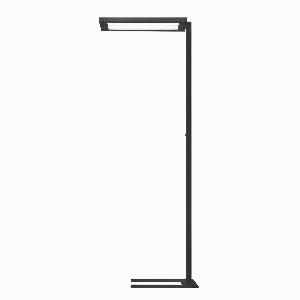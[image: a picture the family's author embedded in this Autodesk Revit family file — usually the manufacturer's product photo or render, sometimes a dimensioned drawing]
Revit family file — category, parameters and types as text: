
# Revit family: lavigo_core_-_dps_9000_840_r_g1_sw_00812472_8bfc
name_source: partatom
category: Lighting Fixtures
units: mm (PartAtom-declared; Revit-internal decimal feet)

## family parameters
Cut with Voids When Loaded = No
Host = Face
Light Source = No
Part Type = Normal
Room Calculation Point = No
Round Connector Dimension = Use Diameter
Shared = No

## types (1)
- LAVIGO.core - DPS 9000/840/R/G1/SW (1 x LED, 8900 lm, 4000K)
    Apparent Load = 62 VA
    Approval mark = CE
    CIE Flux Codes = 59 88 97 35 100
    Color Rendering = 80-89
    Color Temperature = 4000K
    Control Gear = Electronic ballast
    Default Elevation = 1800 mm
    Description = DPS 9000/840/R/G1|Free-standing luminaire|light source: LED Cold white   |work equipment: Electronic ballast DALI|connected load: 220-240 V, 50/60 Hz|Power consumption: approx. 62 W|standby: approx. 0,30|power factor: approx. 0,959|luminous flux: 8900 lm|luminous efficacy: 143 lm/W|light distribution: Direct/indirect|direct ratio: approx. 35 %|color rendering index (CRI): >= 80|chromaticity tolerance:  3 SDCM|technology: Presence and daylight sensor control (PIR)|operation: Rocker switch|luminaire body|material: Steel/plastic|surface: Painted|colour: Black|lamp cover: Polycarbonate (PC), Clear|tubular section|material: Steel tube|surface: Painted|Form: Tubular section upright|colour of tubular section: Black|luminaire base|Form: C-form flat|weight (net): approx. 14.7 kg|mains lead: 3.00 m Mains plug CEE 7/VII|Fastening: Floor standing base|decorative contrast side parts: Black|glare control: Prism aperture|luminance(L65): <= 4400 cd/m|unified glare rating(4H 8H): <=  16|special features: Luminaire head detachable, Direct and indirect light switchable together, Flicker-free, Integrated light and presence sensor PIR, Motion sensor time-out of 15mins~|Approval mark: US~B_0014~VDE - ENEC|
    Frequency = 50 Hz, 60 Hz
    Height = 36 mm
    Lamp = 1 x LED
    Lamp Light Flux = 8900 lm
    Lamp count = 1
    Length = 675 mm
    Luminous efficacy = 144 lm/W
    Manufacturer = Waldmann
    ModVariant = No
    Model = 00812472
    Mounting Place = Floor
    Mounting Type = Freestanding
    Number of Poles = 1
    OnlyDefault = Yes
    Power Factor = 1
    Product Name = LAVIGO.core - DPS 9000/840/R/G1/SW
    Product group = Free standing luminaire
    ProductGroupID = 13
    Protection Class = Protection class I
    Protection Degree = IP 20
    RLX_Detail_Level = 1
    RLX_Emergency_Light_Flux = 0 lm
    RLX_Emergency_Type = 0
    RLX_Emergency_Type_DB = No
    RlxData = <blob elided: 33789 chars, md5=ea5e4615>
    Socket = socket
    Standby Power = 0 W
    System Light Flux = 8900 lm
    System Power = 62 W
    Type Comments = Product without accessories
    Type Image = 121805000-00755032_sw.jpg
    URL = http://relux.com
    VarID = ---
    Voltage = 230 V
    Voltage Range = 220-240 V
    Weight = 0.00 kg
    Width = 320 mm

## geometry (parser evidence)
native form markers: Blend x4, Sweep x13
no freeform markers — native parametric forms only
